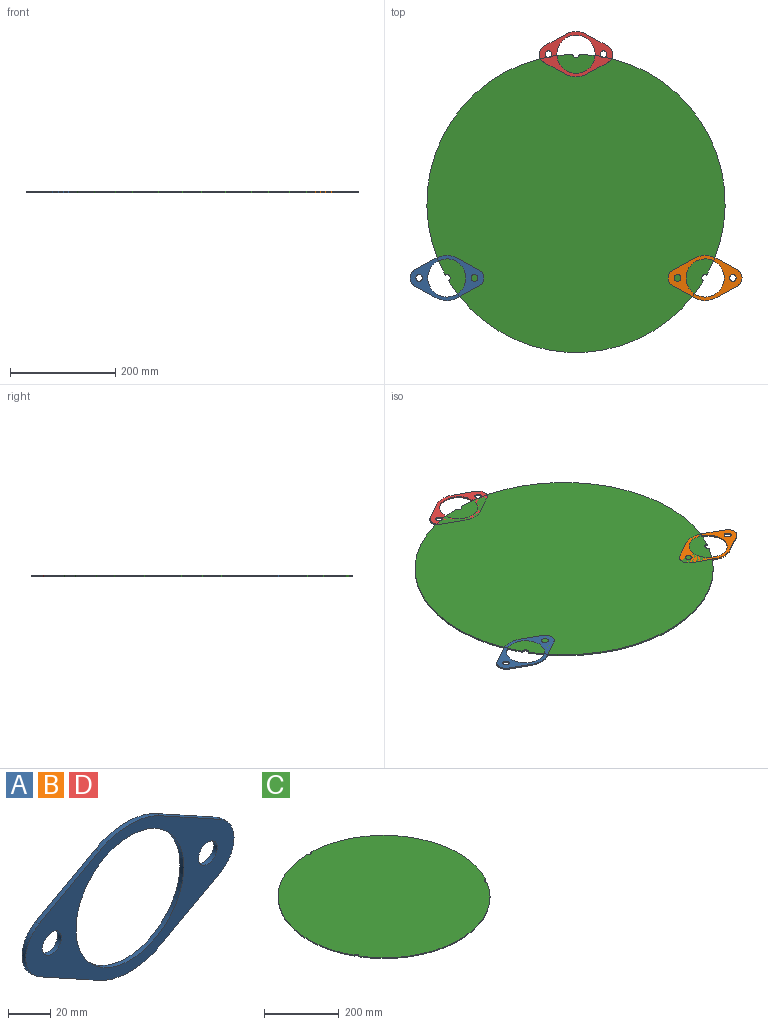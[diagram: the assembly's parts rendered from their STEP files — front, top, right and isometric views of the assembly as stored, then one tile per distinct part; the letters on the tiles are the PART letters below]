
ASSEMBLY  parts=4 mates=3
PART A: 13 faces, bbox 139.7x2.5x85.6 mm
  f0: cylinder r=17.53mm len=30.69mm, axis (0,1,0), area 95mm2, adj f1,f9,f11,f12
  f1: plane 40.12x22.13mm, normal (0.48,0,0.88), area 116.4mm2, adj f0,f2,f11,f12
  f2: cylinder r=42.8mm len=41.34mm, axis (0,1,0), area 109.6mm2, adj f1,f3,f11,f12
  f3: plane 40.12x22.13mm, normal (-0.48,0,0.88), area 116.4mm2, adj f2,f4,f11,f12
  f4: cylinder r=17.53mm len=30.69mm, axis (0,1,0), area 95mm2, adj f3,f5,f11,f12
  f5: plane 40.12x22.13mm, normal (-0.48,0,-0.88), area 116.4mm2, adj f4,f6,f11,f12
  f6: cylinder r=42.8mm len=41.34mm, axis (0,1,0), area 109.6mm2, adj f5,f9,f11,f12
  f7: cylinder r=6.35mm len=12.7mm, axis (0,1,0), area 101.3mm2, adj f11,f12
  f8: cylinder r=6.35mm len=12.7mm, axis (0,1,0), area 101.3mm2, adj f11,f12
  f9: plane 40.12x22.13mm, normal (0.48,0,-0.88), area 116.4mm2, adj f0,f6,f11,f12
  f10: cylinder r=36.2mm len=72.39mm, axis (0,1,0), area 577.6mm2, adj f11,f12
  f11: plane 139.7x85.6mm, normal (0,-1,0), area 3660.6mm2, adj f0,f1,f2,f3,f4,f5,f6,f7
  f12: plane 139.7x85.6mm, normal (0,1,0), area 3660.6mm2, adj f0,f1,f2,f3,f4,f5,f6,f7
PART B: same geometry as A
PART C: 8 faces, bbox 565.8x565.7x2.5 mm
  f0: cylinder r=6.35mm len=11.81mm, axis (0,0,-1), area 50.3mm2, adj f1,f5,f6,f7
  f1: cylinder r=282.91mm len=418.75mm, axis (0,0,-1), area 1472.7mm2, adj f0,f2,f6,f7
  f2: cylinder r=6.35mm len=12.7mm, axis (0,0,-1), area 50.3mm2, adj f1,f3,f6,f7
  f3: cylinder r=282.91mm len=418.75mm, axis (0,0,-1), area 1472.7mm2, adj f2,f4,f6,f7
  f4: cylinder r=6.35mm len=11.81mm, axis (0,0,-1), area 50.3mm2, adj f3,f5,f6,f7
  f5: cylinder r=282.91mm len=483.54mm, axis (0,0,-1), area 1472.7mm2, adj f0,f4,f6,f7
  f6: plane 565.81x565.74mm, normal (0,0,1), area 251251.6mm2, adj f0,f1,f2,f3,f4,f5
  f7: plane 565.81x565.74mm, normal (0,0,-1), area 251251.6mm2, adj f0,f1,f2,f3,f4,f5
PART D: same geometry as A
PLACE A rot(axis=(1,0,0),90deg) t=(-245,-141.45,2.54)mm
PLACE B rot(axis=(1,0,0),90deg) t=(245,-141.45,2.54)mm
PLACE C at identity
PLACE D rot(axis=(1,0,0),90deg) t=(0,282.91,2.54)mm
MATE fastened A.f2 <-> C.f4  axis (0,0,1) through (-245,-141.45,2.54)mm
MATE fastened B.f2 <-> C.f0  axis (0,0,1) through (245,-141.45,2.54)mm
MATE fastened D.f2 <-> C.f2  axis (0,0,1) through (0,282.91,2.54)mm
